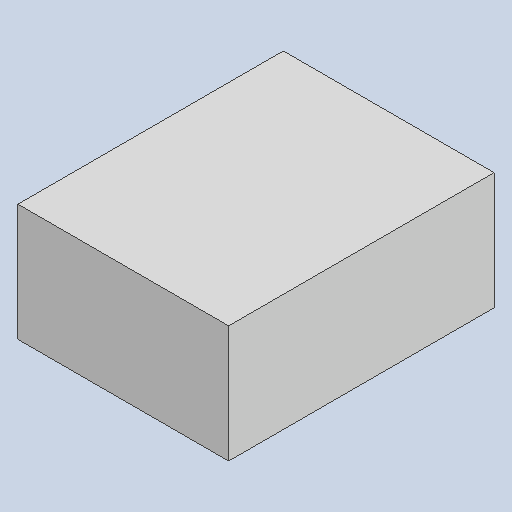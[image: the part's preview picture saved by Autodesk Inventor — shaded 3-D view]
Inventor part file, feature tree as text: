
AUTODESK INVENTOR PART (.ipt)
format: ipt  version: 2022 (Build 260153000, 153)  size: 82,944 bytes
history: native  units: mm
features: other x3, sketch x1
ambient origin geometry x8: Origin, YZ Plane, XZ Plane, XY Plane, X Axis, Y Axis, Z Axis, Center Point
bodies: Solid1 (feature_tree)
feature tree (4):
  other  "ktir.ipt"
  other  "Solid1::ktir.ipt"
  other  "TaggingFeature1"
  sketch  "Sketch1"  dims[d0=10.0mm]
